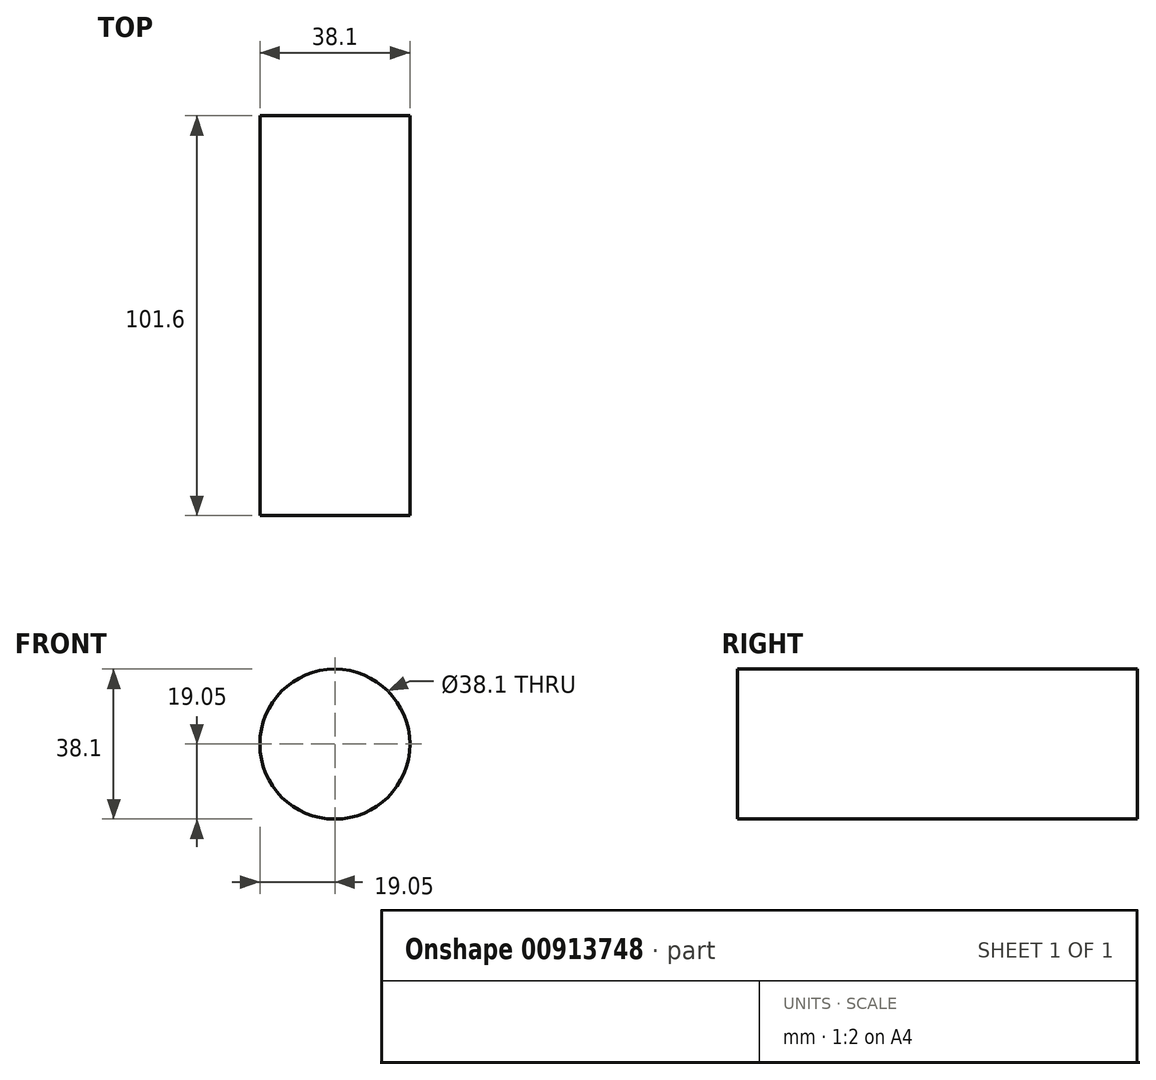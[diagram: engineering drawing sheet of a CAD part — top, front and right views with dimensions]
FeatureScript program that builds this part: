
annotation { "Feature Type Name" : "Feature", "Feature Type Description" : "" }
export const myFeature = defineFeature(function(context is Context, id is Id, definition is map)
    precondition{}
    {
        {
            var Q0;
            Q0=qCreatedBy(makeId("Front.planeOp"),FACE);
            var sketch = newSketch(context, id + "F0", { "sketchPlane" : qUnion([Q0])});
            skCircle(sketch, "E0", {"center": v(0, 0) * mm, "radius": 19.05 * mm});
            skSolve(sketch);
        }
        {
            var Q0;
            Q0=sQuery(id+"F0.wireOp",EDGE,"E0");
            extrude(context, id + "F1", {"bodyType" : ToolBodyType.SURFACE, "surfaceEntities" : qUnion([Q0]), "oppositeDirection" : true, "depth" : 101.6 * mm, "offsetDistance" : 25.4 * mm});
        }
    });
